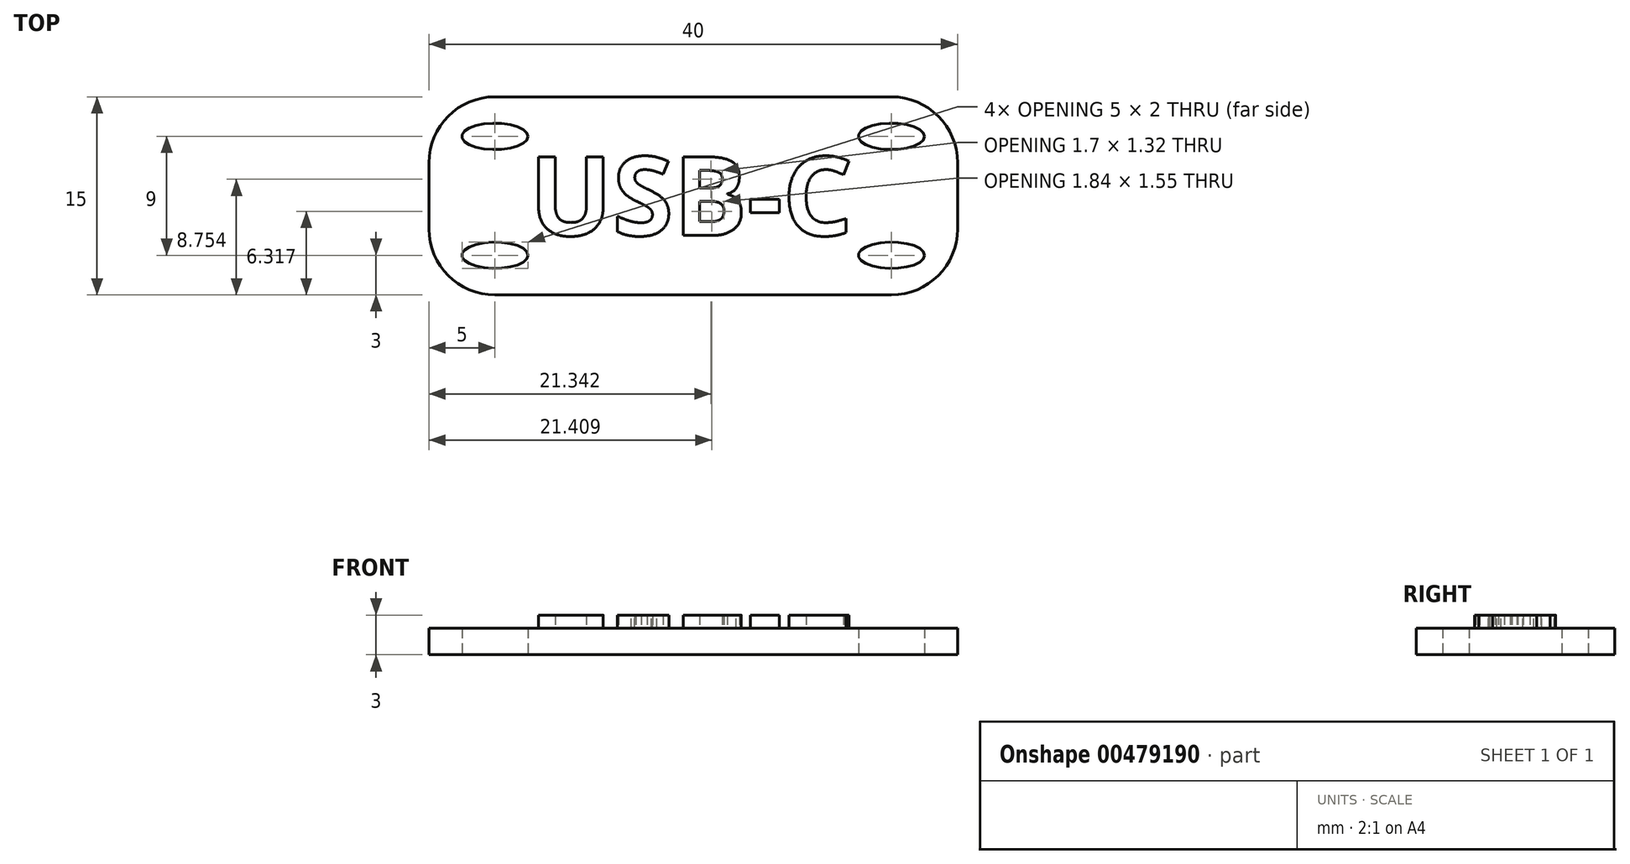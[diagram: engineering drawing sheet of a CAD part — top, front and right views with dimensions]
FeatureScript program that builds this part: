
annotation { "Feature Type Name" : "Feature", "Feature Type Description" : "" }
export const myFeature = defineFeature(function(context is Context, id is Id, definition is map)
    precondition{}
    {
        {
            var Q0;
            Q0=qCreatedBy(makeId("Top.planeOp"),FACE);
            var sketch = newSketch(context, id + "F0", { "sketchPlane" : qUnion([Q0])});
            skLineSegment(sketch, "E0.bottom", {"start": v(20, -7.5) * mm, "end": v(-20, -7.5) * mm});
            skLineSegment(sketch, "E0.top", {"start": v(20, 7.5) * mm, "end": v(-20, 7.5) * mm});
            skLineSegment(sketch, "E0.left", {"start": v(20, -7.5) * mm, "end": v(20, 7.5) * mm});
            skLineSegment(sketch, "E0.right", {"start": v(-20, -7.5) * mm, "end": v(-20, 7.5) * mm});
            skPoint(sketch, "E0.middle", {"position": v(0, 0) * mm});
            skLineSegment(sketch, "E1", {"start": v(-20, -4.5) * mm, "end": v(20, -4.5) * mm, "construction": true});
            skPoint(sketch, "E2", {"position": v(-15, -4.5) * mm});
            skEllipse(sketch, "E3", {"center": v(-15, -4.5) * mm, "majorRadius": 2.5 * mm, "minorRadius": 1 * mm, "majorAxis": v(1, 0)});
            skEllipse(sketch, "E4.1.0.0", {"center": v(15, -4.5) * mm, "majorRadius": 2.5 * mm, "minorRadius": 1 * mm, "majorAxis": v(1, 0)});
            skLineSegment(sketch, "E4.direction1", {"start": v(-15, -4.5) * mm, "end": v(15, -4.5) * mm, "construction": true});
            skLineSegment(sketch, "E5", {"start": v(20, 0) * mm, "end": v(-20, 0) * mm, "construction": true});
            skEllipse(sketch, "E6.MirrorC", {"center": v(15, 4.5) * mm, "majorRadius": 2.5 * mm, "minorRadius": 1 * mm, "majorAxis": v(1, 0)});
            skEllipse(sketch, "E7.MirrorC", {"center": v(-15, 4.5) * mm, "majorRadius": 2.5 * mm, "minorRadius": 1 * mm, "majorAxis": v(1, 0)});
            skSolve(sketch);
        }
        {
            var Q0;
            Q0=makeQuery(id+"F0.imprint","IMPRINT",FACE,{"disambiguationData":[TD([[makeQuery(id+"F0.imprint","IMPRINT",EDGE,{"derivedFrom":sQuery(id+"F0.wireOp",EDGE,"E0.bottom")}),-1.0]])]});
            extrude(context, id + "F1", {"entities" : qUnion([Q0]), "depth" : 2 * mm});
        }
        {
            var Q0;
            Q0=makeQuery(id+"F1.opExtrude","CAP_FACE",FACE,{"disambiguationData":[OSD([sQuery(id+"F0.wireOp",EDGE,"E0.bottom"),sQuery(id+"F0.wireOp",EDGE,"E0.top"),sQuery(id+"F0.wireOp",EDGE,"E0.left"),sQuery(id+"F0.wireOp",EDGE,"E0.right"),sQuery(id+"F0.wireOp",EDGE,"E3"),sQuery(id+"F0.wireOp",EDGE,"E4.1.0.0"),sQuery(id+"F0.wireOp",EDGE,"E6.MirrorC"),sQuery(id+"F0.wireOp",EDGE,"E7.MirrorC")])],"isStart":false});
            var sketch = newSketch(context, id + "F2", { "sketchPlane" : qUnion([Q0])});
            skText(sketch, "E8", { "text": "USB-C", "fontName": "OpenSans-Bold.ttf"});
            const initialGuessF2  = {"E8": [-0.01241, -0.003, 1, 0, 0.006]};
            skSetInitialGuess(sketch, initialGuessF2);
            skSolve(sketch);
        }
        {
            var Q0;
            Q0=qSketchRegion(id+"F2",true);
            extrude(context, id + "F3", {"entities" : qUnion([Q0]), "depth" : 1 * mm});
        }
        {
            var Q0;
            Q0=makeQuery(id+"F1.opExtrude","SWEPT_EDGE",EDGE,{"disambiguationData":[OSD([sQuery(id+"F0.wireOp",EDGE,"E0.bottom"),sQuery(id+"F0.wireOp",EDGE,"E0.right")])]});
            var Q1;
            Q1=makeQuery(id+"F1.opExtrude","SWEPT_EDGE",EDGE,{"disambiguationData":[OSD([sQuery(id+"F0.wireOp",EDGE,"E0.bottom"),sQuery(id+"F0.wireOp",EDGE,"E0.left")])]});
            var Q2;
            Q2=makeQuery(id+"F1.opExtrude","SWEPT_EDGE",EDGE,{"disambiguationData":[OSD([sQuery(id+"F0.wireOp",EDGE,"E0.top"),sQuery(id+"F0.wireOp",EDGE,"E0.left")])]});
            var Q3;
            Q3=makeQuery(id+"F1.opExtrude","SWEPT_EDGE",EDGE,{"disambiguationData":[OSD([sQuery(id+"F0.wireOp",EDGE,"E0.top"),sQuery(id+"F0.wireOp",EDGE,"E0.right")])]});
            fillet(context, id + "F4", {"entities" : qUnion([Q0, Q1, Q2, Q3]), "radius" : 5 * mm, "tangentPropagation" : true, "allowEdgeOverflow" : false});
        }
    });
